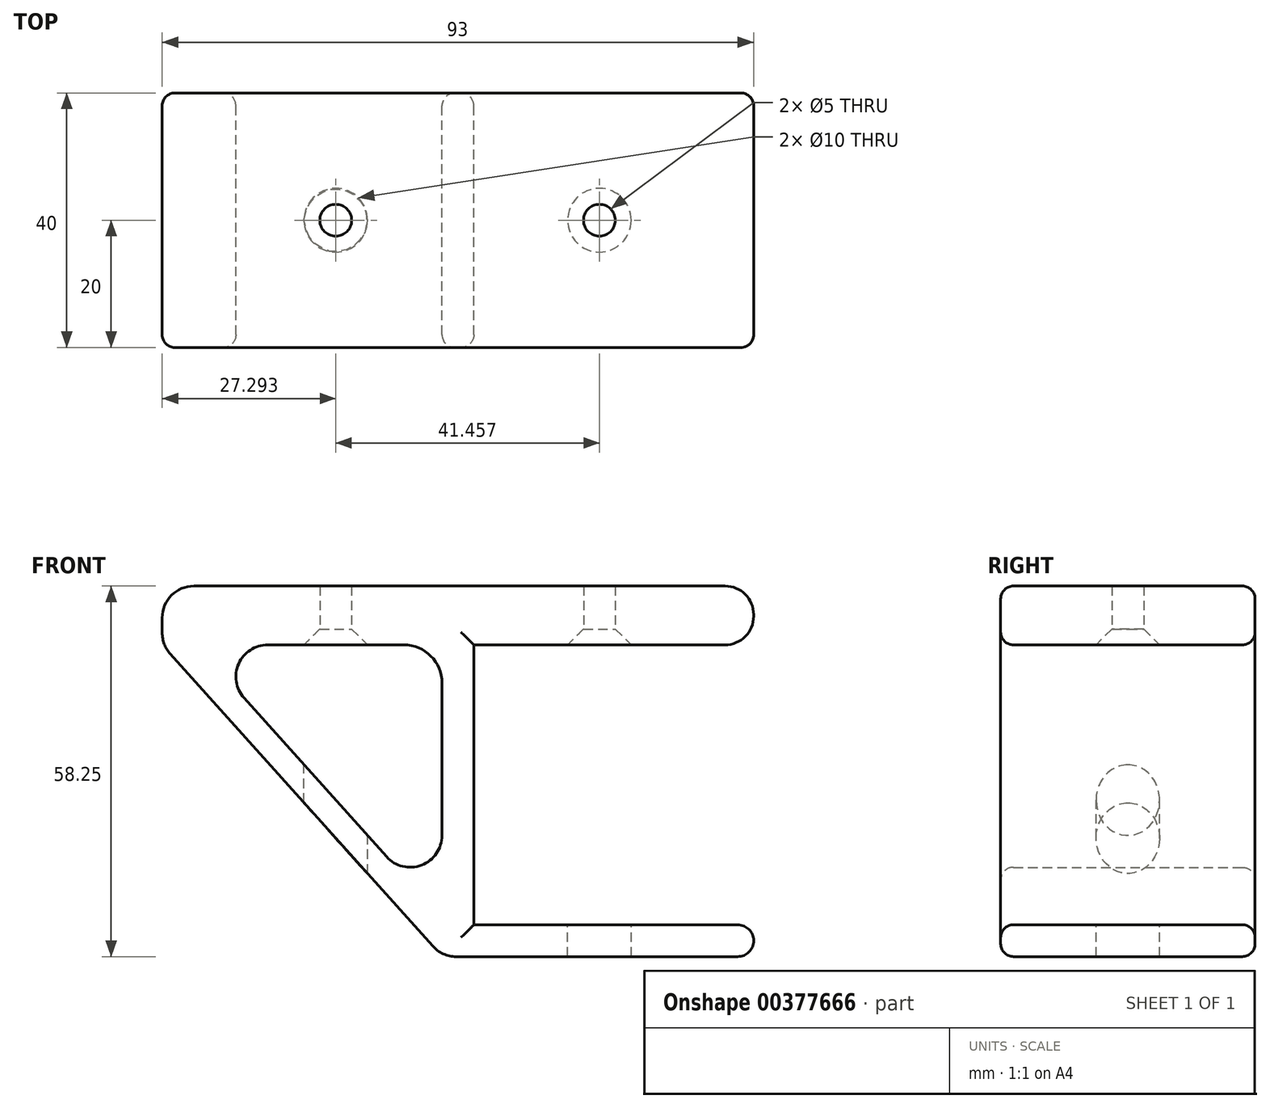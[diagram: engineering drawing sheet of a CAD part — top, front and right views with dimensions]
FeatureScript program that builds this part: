
annotation { "Feature Type Name" : "Feature", "Feature Type Description" : "" }
export const myFeature = defineFeature(function(context is Context, id is Id, definition is map)
    precondition{}
    {
        {
            var Q0;
            Q0=qCreatedBy(makeId("Front.planeOp"),FACE);
            var sketch = newSketch(context, id + "F0", { "sketchPlane" : qUnion([Q0])});
            skLineSegment(sketch, "E0", {"start": v(-44, 0) * mm, "end": v(44.5, 0) * mm});
            skLineSegment(sketch, "E1", {"start": v(-44, 0) * mm, "end": v(-44, -9.25) * mm});
            skLineSegment(sketch, "E2", {"start": v(-38.62, -9.25) * mm, "end": v(-6, -9.25) * mm});
            skLineSegment(sketch, "E3", {"start": v(49, -4.75) * mm, "end": v(49, -4.5) * mm});
            skLineSegment(sketch, "E4", {"start": v(0, -15.25) * mm, "end": v(0, -52.26) * mm});
            skLineSegment(sketch, "E5", {"start": v(0, -58.25) * mm, "end": v(46.5, -58.25) * mm});
            skLineSegment(sketch, "E6", {"start": v(5, -53.25) * mm, "end": v(5, -9.25) * mm});
            skLineSegment(sketch, "E7.trimOffspring", {"start": v(5, -9.25) * mm, "end": v(44.5, -9.25) * mm});
            skPoint(sketch, "E8.visualSharp", {"position": v(0, -9.25) * mm});
            skArc(sketch, "E8.filletArc", {"start": v(0, -15.25) * mm, "mid": v(-1.76, -11) * mm, "end": v(-6, -9.25) * mm});
            skPoint(sketch, "E9.visualSharp", {"position": v(49, -9.25) * mm});
            skArc(sketch, "E9.filletArc", {"start": v(44.5, -9.25) * mm, "mid": v(47.68, -7.93) * mm, "end": v(49, -4.75) * mm});
            skPoint(sketch, "E10.visualSharp", {"position": v(49, 0) * mm});
            skArc(sketch, "E10.filletArc", {"start": v(49, -4.5) * mm, "mid": v(47.68, -1.32) * mm, "end": v(44.5, 0) * mm});
            skLineSegment(sketch, "E11", {"start": v(5, -53.25) * mm, "end": v(46.5, -53.25) * mm});
            skLineSegment(sketch, "E12", {"start": v(49, -55.75) * mm, "end": v(49, -55.75) * mm});
            skPoint(sketch, "E13.visualSharp", {"position": v(49, -53.25) * mm});
            skArc(sketch, "E13.filletArc", {"start": v(49, -55.75) * mm, "mid": v(48.27, -53.98) * mm, "end": v(46.5, -53.25) * mm});
            skPoint(sketch, "E14.visualSharp", {"position": v(49, -58.25) * mm});
            skArc(sketch, "E14.filletArc", {"start": v(46.5, -58.25) * mm, "mid": v(48.27, -57.52) * mm, "end": v(49, -55.75) * mm});
            skLineSegment(sketch, "E15", {"start": v(0, -58.25) * mm, "end": v(-44, -9.25) * mm});
            skLineSegment(sketch, "E16", {"start": v(-38.62, -9.25) * mm, "end": v(0, -52.26) * mm});
            skSolve(sketch);
        }
        {
            var Q0;
            Q0=makeQuery(id+"F0.imprint","IMPRINT",FACE,{"disambiguationData":[TD([[makeQuery(id+"F0.imprint","IMPRINT",EDGE,{"derivedFrom":sQuery(id+"F0.wireOp",EDGE,"E0")}),-1.0]])]});
            extrude(context, id + "F1", {"entities" : qUnion([Q0]), "endBound" : BoundingType.SYMMETRIC, "depth" : 40 * mm});
        }
        {
            var Q0;
            Q0=makeQuery(id+"F1.opExtrude","SWEPT_EDGE",EDGE,{"disambiguationData":[OSD([sQuery(id+"F0.wireOp",EDGE,"E0"),sQuery(id+"F0.wireOp",EDGE,"E1")])]});
            var Q1;
            Q1=makeQuery(id+"F1.opExtrude","SWEPT_EDGE",EDGE,{"disambiguationData":[OSD([sQuery(id+"F0.wireOp",EDGE,"E1"),sQuery(id+"F0.wireOp",EDGE,"E15")])]});
            var Q2;
            Q2=makeQuery(id+"F1.opExtrude","SWEPT_EDGE",EDGE,{"disambiguationData":[OSD([sQuery(id+"F0.wireOp",EDGE,"E2"),sQuery(id+"F0.wireOp",EDGE,"E16")])]});
            var Q3;
            Q3=makeQuery(id+"F1.opExtrude","SWEPT_EDGE",EDGE,{"disambiguationData":[OSD([sQuery(id+"F0.wireOp",EDGE,"E4"),sQuery(id+"F0.wireOp",EDGE,"E16")])]});
            var Q4;
            Q4=makeQuery(id+"F1.opExtrude","SWEPT_EDGE",EDGE,{"disambiguationData":[OSD([sQuery(id+"F0.wireOp",EDGE,"E5"),sQuery(id+"F0.wireOp",EDGE,"E15")])]});
            fillet(context, id + "F2", {"entities" : qUnion([Q0, Q1, Q2, Q3, Q4]), "radius" : 5 * mm, "tangentPropagation" : true, "allowEdgeOverflow" : false});
        }
        {
            var Q0;
            Q0=makeQuery(id+"F1.opExtrude","CAP_EDGE",EDGE,{"disambiguationData":[OSD([sQuery(id+"F0.wireOp",EDGE,"E7.trimOffspring")])],"isStart":false});
            var Q1;
            Q1=makeQuery(id+"F1.opExtrude","CAP_EDGE",EDGE,{"disambiguationData":[OSD([sQuery(id+"F0.wireOp",EDGE,"E11")])],"isStart":false});
            var Q2;
            Q2=makeQuery(id+"F1.opExtrude","CAP_EDGE",EDGE,{"disambiguationData":[OSD([sQuery(id+"F0.wireOp",EDGE,"E7.trimOffspring")])],"isStart":true});
            var Q3;
            Q3=makeQuery(id+"F1.opExtrude","CAP_EDGE",EDGE,{"disambiguationData":[OSD([sQuery(id+"F0.wireOp",EDGE,"E2")])],"isStart":false});
            var Q4;
            Q4=makeQuery(id+"F1.opExtrude","CAP_EDGE",EDGE,{"disambiguationData":[OSD([sQuery(id+"F0.wireOp",EDGE,"E6")])],"isStart":false});
            var Q5;
            Q5=makeQuery(id+"F1.opExtrude","CAP_EDGE",EDGE,{"disambiguationData":[OSD([sQuery(id+"F0.wireOp",EDGE,"E6")])],"isStart":true});
            var Q6;
            Q6=makeQuery(id+"F1.opExtrude","CAP_EDGE",EDGE,{"disambiguationData":[OSD([sQuery(id+"F0.wireOp",EDGE,"E2")])],"isStart":true});
            fillet(context, id + "F3", {"entities" : qUnion([Q0, Q1, Q2, Q3, Q4, Q5, Q6]), "radius" : 2 * mm, "tangentPropagation" : true, "allowEdgeOverflow" : false});
        }
        {
            var Q0;
            Q0=makeQuery(id+"F1.opExtrude","SWEPT_FACE",FACE,{"disambiguationData":[OSD([sQuery(id+"F0.wireOp",EDGE,"E7.trimOffspring")])]});
            var sketch = newSketch(context, id + "F4", { "sketchPlane" : qUnion([Q0])});
            skLineSegment(sketch, "E17", {"start": v(44.5, 18) * mm, "end": v(5, -18) * mm});
            skLineSegment(sketch, "E18", {"start": v(5, -18) * mm, "end": v(44.5, -18) * mm});
            skLineSegment(sketch, "E19", {"start": v(44.5, -18) * mm, "end": v(5, 18) * mm});
            skPoint(sketch, "E20", {"position": v(24.75, 0) * mm});
            skSolve(sketch);
        }
        {
            var Q0;
            Q0=makeQuery(id+"F1.opExtrude","SWEPT_FACE",FACE,{"disambiguationData":[OSD([sQuery(id+"F0.wireOp",EDGE,"E2")])]});
            var sketch = newSketch(context, id + "F5", { "sketchPlane" : qUnion([Q0])});
            skLineSegment(sketch, "E21", {"start": v(-6, 18) * mm, "end": v(-27.41, -18) * mm});
            skLineSegment(sketch, "E22", {"start": v(-6, -18) * mm, "end": v(-27.41, 18) * mm});
            skPoint(sketch, "E23", {"position": v(-16.7, 0) * mm});
            skSolve(sketch);
        }
        {
            var Q0;
            Q0=sQuery(id+"F4.wireOp",VERTEX,"E20");
            var Q1;
            Q1=sQuery(id+"F5.wireOp",VERTEX,"E23");
            var Q2;
            Q2=makeQuery(id+"F1.opExtrude","SWEPT_BODY",BODY,{"disambiguationData":[OSD([sQuery(id+"F0.wireOp",EDGE,"E0"),sQuery(id+"F0.wireOp",EDGE,"E1"),sQuery(id+"F0.wireOp",EDGE,"E2"),sQuery(id+"F0.wireOp",EDGE,"E3"),sQuery(id+"F0.wireOp",EDGE,"E4"),sQuery(id+"F0.wireOp",EDGE,"E5"),sQuery(id+"F0.wireOp",EDGE,"E6"),sQuery(id+"F0.wireOp",EDGE,"E7.trimOffspring"),sQuery(id+"F0.wireOp",EDGE,"E8.filletArc"),sQuery(id+"F0.wireOp",EDGE,"E9.filletArc"),sQuery(id+"F0.wireOp",EDGE,"E10.filletArc"),sQuery(id+"F0.wireOp",EDGE,"E11"),sQuery(id+"F0.wireOp",EDGE,"E13.filletArc"),sQuery(id+"F0.wireOp",EDGE,"E14.filletArc"),sQuery(id+"F0.wireOp",EDGE,"E15"),sQuery(id+"F0.wireOp",EDGE,"E16")])]});
            hole(context, id + "F6", {"style" : HoleStyle.C_SINK, "endStyle" : HoleEndStyle.BLIND, "holeDiameter" : 5 * mm, "cSinkDiameter" : 10 * mm, "cSinkAngle" : 90 * degree, "holeDepth" : 10 * mm, "isTappedThrough" : true, "tappedDepth" : 12 * mm, "tapClearance" : 3, "startFromSketch" : true, "locations" : qUnion([Q0, Q1]), "scope" : qUnion([Q2])});
        }
        {
            var Q0;
            Q0=sQuery(id+"F4.wireOp",VERTEX,"E20");
            var Q1;
            Q1=sQuery(id+"F5.wireOp",VERTEX,"E23");
            var Q2;
            Q2=makeQuery(id+"F1.opExtrude","SWEPT_BODY",BODY,{"disambiguationData":[OSD([sQuery(id+"F0.wireOp",EDGE,"E0"),sQuery(id+"F0.wireOp",EDGE,"E1"),sQuery(id+"F0.wireOp",EDGE,"E2"),sQuery(id+"F0.wireOp",EDGE,"E3"),sQuery(id+"F0.wireOp",EDGE,"E4"),sQuery(id+"F0.wireOp",EDGE,"E5"),sQuery(id+"F0.wireOp",EDGE,"E6"),sQuery(id+"F0.wireOp",EDGE,"E7.trimOffspring"),sQuery(id+"F0.wireOp",EDGE,"E8.filletArc"),sQuery(id+"F0.wireOp",EDGE,"E9.filletArc"),sQuery(id+"F0.wireOp",EDGE,"E10.filletArc"),sQuery(id+"F0.wireOp",EDGE,"E11"),sQuery(id+"F0.wireOp",EDGE,"E13.filletArc"),sQuery(id+"F0.wireOp",EDGE,"E14.filletArc"),sQuery(id+"F0.wireOp",EDGE,"E15"),sQuery(id+"F0.wireOp",EDGE,"E16")])]});
            hole(context, id + "F7", {"style" : HoleStyle.SIMPLE, "endStyle" : HoleEndStyle.THROUGH, "oppositeDirection" : true, "holeDiameter" : 10 * mm, "isTappedThrough" : true, "tappedDepth" : 12 * mm, "tapClearance" : 3, "startFromSketch" : true, "locations" : qUnion([Q0, Q1]), "scope" : qUnion([Q2])});
        }
    });
